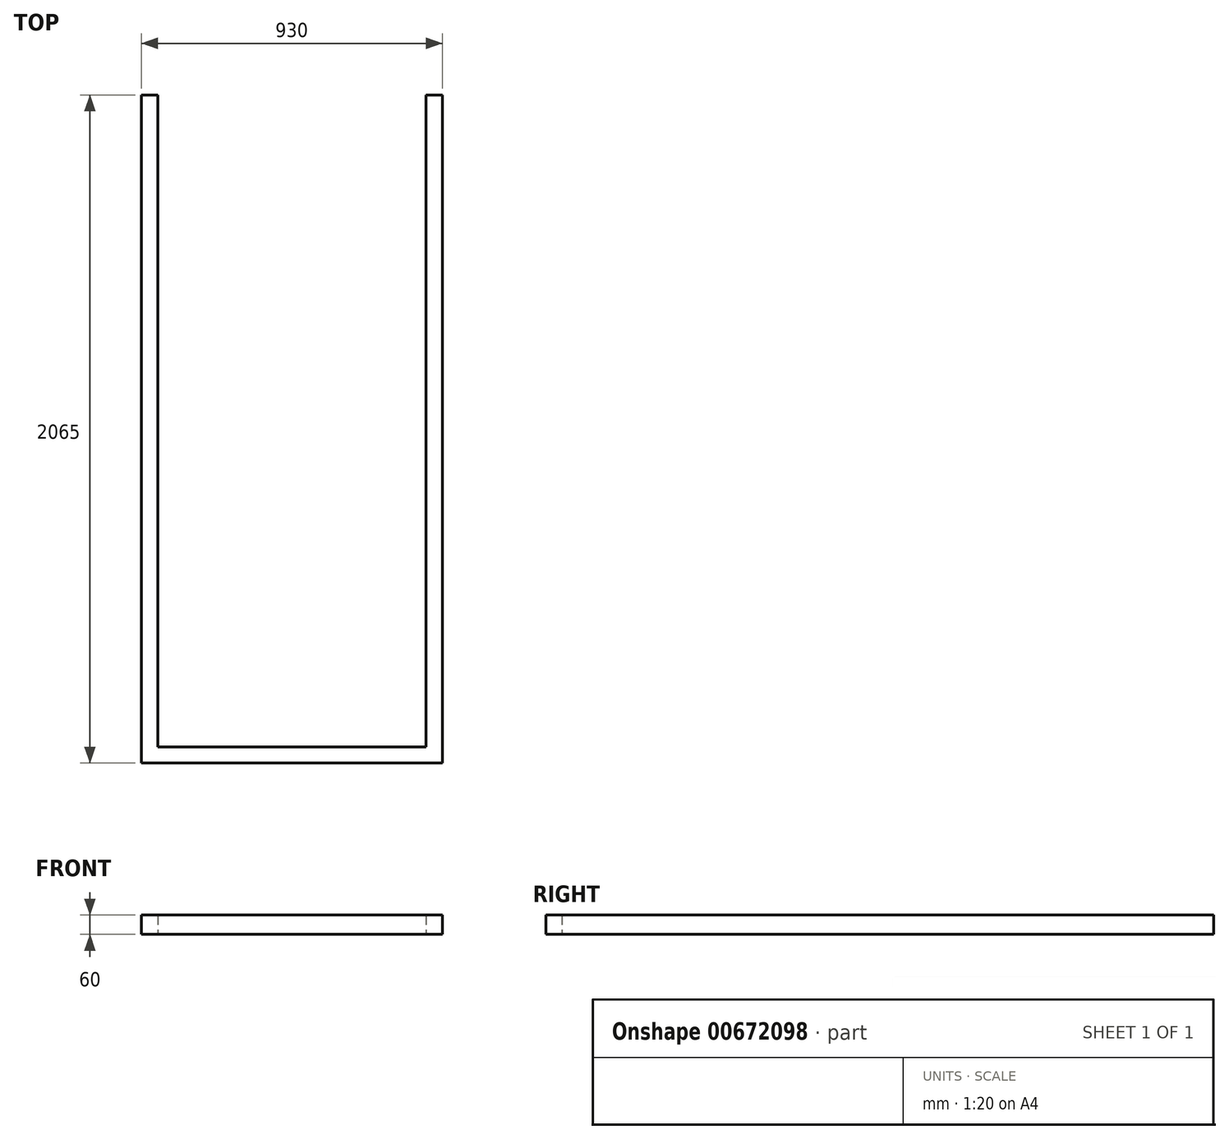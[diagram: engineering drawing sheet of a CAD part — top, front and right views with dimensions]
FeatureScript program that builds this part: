
annotation { "Feature Type Name" : "Feature", "Feature Type Description" : "" }
export const myFeature = defineFeature(function(context is Context, id is Id, definition is map)
    precondition{}
    {
        {
            var Q0;
            Q0=qCreatedBy(makeId("Top.planeOp"),FACE);
            var sketch = newSketch(context, id + "F0", { "sketchPlane" : qUnion([Q0])});
            skLineSegment(sketch, "E0.bottom", {"start": v(0, 0) * mm, "end": v(-930, 0) * mm});
            skLineSegment(sketch, "E0.top", {"start": v(0, 2065) * mm, "end": v(-50, 2065) * mm});
            skLineSegment(sketch, "E0.left", {"start": v(0, 0) * mm, "end": v(0, 2065) * mm});
            skLineSegment(sketch, "E0.right", {"start": v(-930, 0) * mm, "end": v(-930, 2065) * mm});
            skLineSegment(sketch, "E1.0", {"start": v(-50, 50) * mm, "end": v(-880, 50) * mm});
            skLineSegment(sketch, "E1.1", {"start": v(-50, 50) * mm, "end": v(-50, 2065) * mm});
            skLineSegment(sketch, "E1.3", {"start": v(-880, 50) * mm, "end": v(-880, 2065) * mm});
            skLineSegment(sketch, "E2.trimOffspring", {"start": v(-880, 2065) * mm, "end": v(-930, 2065) * mm});
            skSolve(sketch);
        }
        {
            var Q0;
            Q0 = qSketchRegion(id + "F0", true);
            extrude(context, id + "F1", {"entities" : qUnion([Q0]), "endBound" : BoundingType.SYMMETRIC, "depth" : 60 * mm, "offsetDistance" : 25 * mm});
        }
    });
